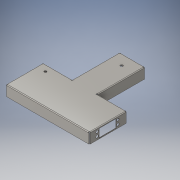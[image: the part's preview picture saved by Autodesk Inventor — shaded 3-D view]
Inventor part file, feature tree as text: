
AUTODESK INVENTOR PART (.ipt)
format: ipt  version: 2016 (Build 200138000, 138)  size: 407,040 bytes
history: native  units: in
note: dims shown in document units (in); Inventor stores cm internally (conversion verified against a paired STEP export)
features: other x12, sketch x10, sheet_metal_op x6
ambient origin geometry x8: Origin, YZ Plane, XZ Plane, XY Plane, X Axis, Y Axis, Z Axis, Center Point
bodies: Solid1 (feature_tree)
feature tree (28):
  sheet_metal_op  "Face1"
  sheet_metal_op  "Face2"
  sheet_metal_op  "Flange1"
  sketch  "Sketch9"  dims[d9=3.4374in]
  sketch  "Sketch18"  dims[d11=2.799in]
  sketch  "Sketch21"  dims[d13=0.034in]
  sketch  "Sketch22"  dims[d14=0.034in]
  sketch  "Sketch2"  dims[d0=2.3in]
  other  "Plate1"
  sketch  "Sketch4"  dims[d1=8.0in]
  other  "Plate2"
  sheet_metal_op  "Bend1"
  sketch  "Sketch5"  dims[d2=0.034in]
  other  "Plate3"
  sheet_metal_op  "Bend2"
  sheet_metal_op  "Corner1"
  sketch  "Sketch13"  dims[d10=2.7993in]
  sketch  "Sketch20"  dims[d12=3.4374in]
  sketch  "Sketch23"  dims[d15=0.017in d16=0.068in d17=0.034in d18=0.034in d19=0.017in d20=0.068in d21=0.034in d22=1.0in d23=90.0deg d24=0.034in d25=0.136in d26=0.034in d27=0.034in d39=0.25in d40=0.034in d41=0.0in d42=0.8in d53=0.917in d55=0.034in d56=0.0in d57=0.917in d64=45.0deg d65=0.034in d66=0.0in d67=0.917in d71=1.625in d72=12.0in d73=0.0in d74=12.0in d75=0.0in d76=0.034in d77=0.0in d78=0.034in d79=0.0in d80=0.2307in d81=0.034in d82=0.0in]
  other  "Cut5"
  other  "Cut7"
  other  "Cut10"
  other  "Cut12"
  other  "Cut13"
  other  "Cut14"
  other  "Cut15"
  other  "Cut16"
  other  "Definition1"
